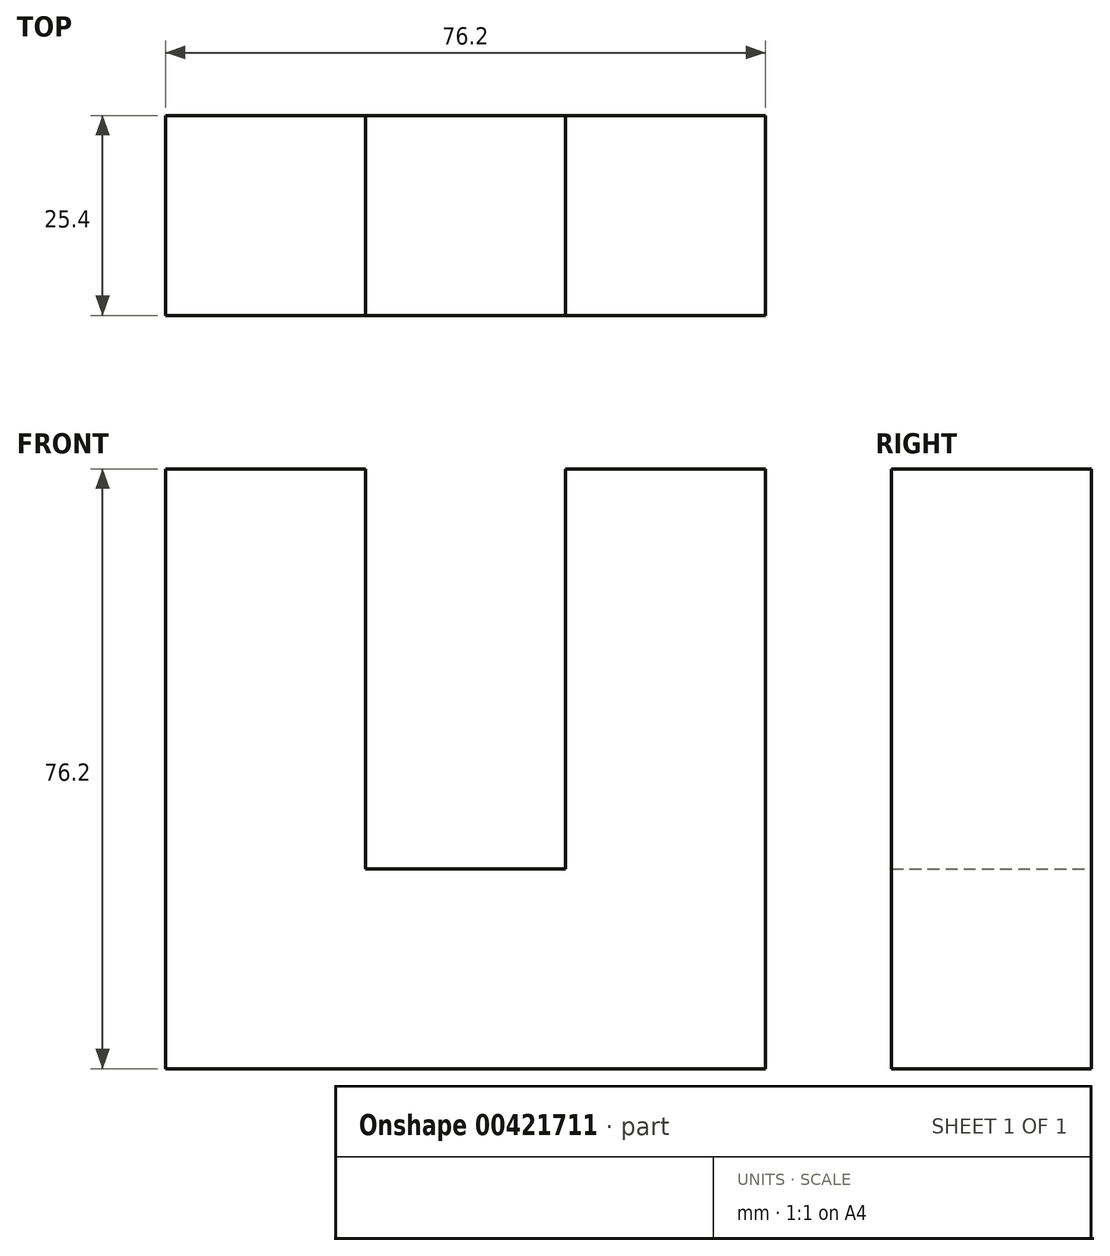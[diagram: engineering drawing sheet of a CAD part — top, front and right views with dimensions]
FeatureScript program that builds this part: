
annotation { "Feature Type Name" : "Feature", "Feature Type Description" : "" }
export const myFeature = defineFeature(function(context is Context, id is Id, definition is map)
    precondition{}
    {
        {
            var Q0;
            Q0=qCreatedBy(makeId("Front.planeOp"),FACE);
            var sketch = newSketch(context, id + "F0", { "sketchPlane" : qUnion([Q0])});
            skLineSegment(sketch, "E0", {"start": v(-10.14, 76.2) * mm, "end": v(-35.54, 76.2) * mm});
            skLineSegment(sketch, "E1", {"start": v(-35.54, 0) * mm, "end": v(-35.54, 76.2) * mm});
            skLineSegment(sketch, "E2", {"start": v(-35.54, 0) * mm, "end": v(40.66, 0) * mm});
            skLineSegment(sketch, "E3", {"start": v(40.66, 0) * mm, "end": v(40.66, 76.2) * mm});
            skLineSegment(sketch, "E4", {"start": v(40.66, 76.2) * mm, "end": v(15.26, 76.2) * mm});
            skLineSegment(sketch, "E5", {"start": v(15.26, 76.2) * mm, "end": v(15.26, 25.4) * mm});
            skLineSegment(sketch, "E6", {"start": v(-10.14, 76.2) * mm, "end": v(-10.14, 25.4) * mm});
            skLineSegment(sketch, "E7", {"start": v(-10.14, 25.4) * mm, "end": v(15.26, 25.4) * mm});
            skSolve(sketch);
        }
        {
            var Q0;
            Q0=makeQuery(id+"F0.imprint","IMPRINT",FACE,{"disambiguationData":[TD([[makeQuery(id+"F0.imprint","IMPRINT",EDGE,{"derivedFrom":sQuery(id+"F0.wireOp",EDGE,"E0")}),1.0]])]});
            extrude(context, id + "F1", {"entities" : qUnion([Q0]), "depth" : 25.4 * mm});
        }
    });
